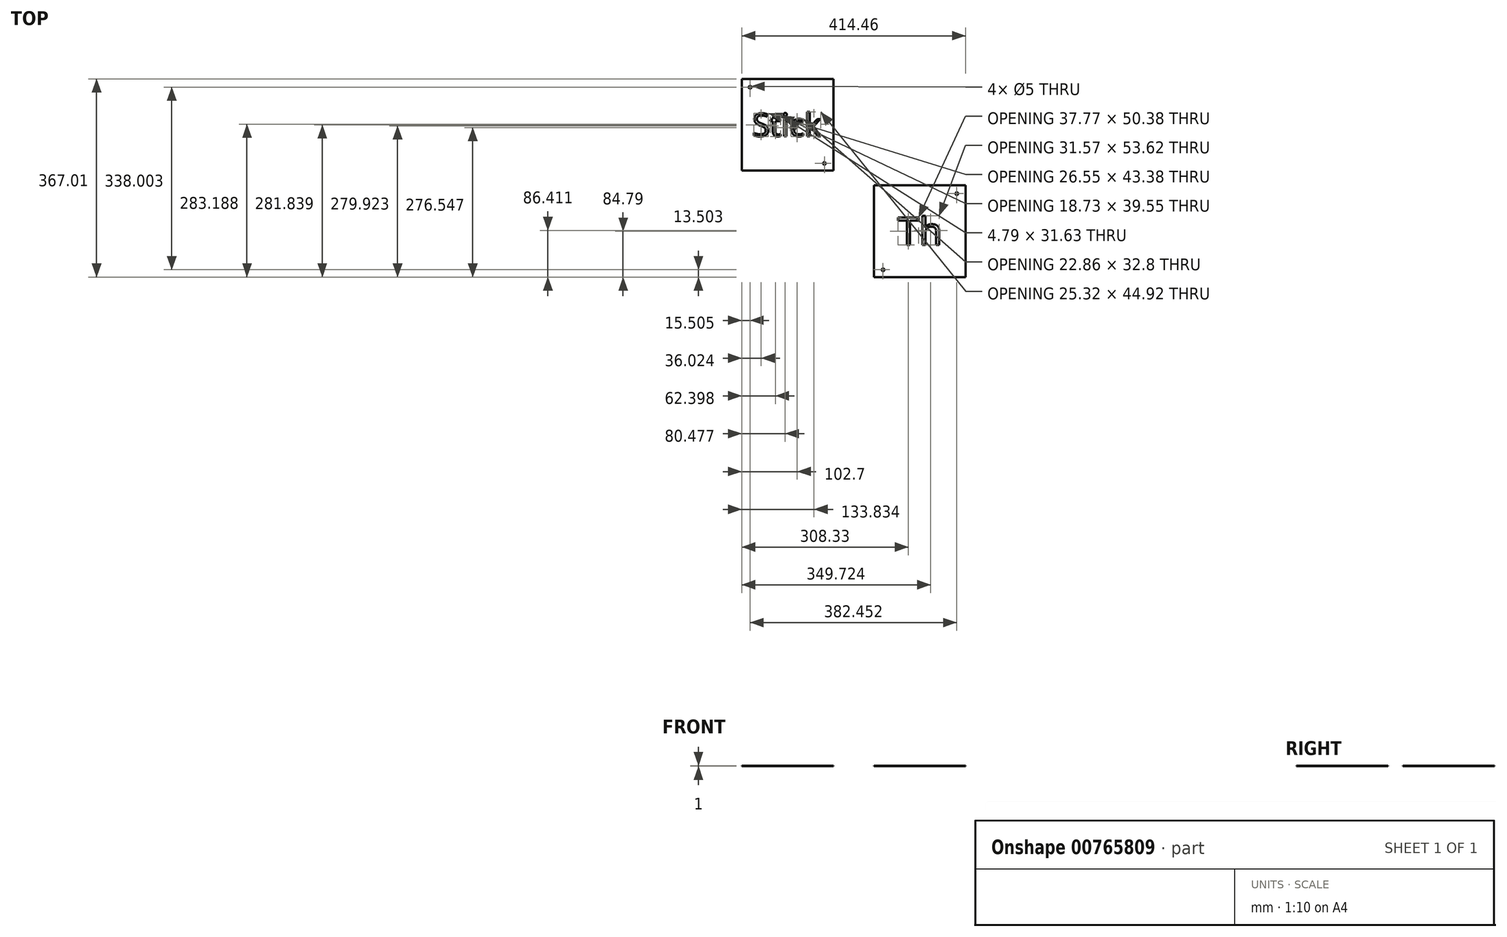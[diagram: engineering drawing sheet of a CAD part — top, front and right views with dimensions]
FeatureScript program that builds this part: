
annotation { "Feature Type Name" : "Feature", "Feature Type Description" : "" }
export const myFeature = defineFeature(function(context is Context, id is Id, definition is map)
    precondition{}
    {
        {
            var Q0;
            Q0=qCreatedBy(makeId("Top.planeOp"),FACE);
            var sketch = newSketch(context, id + "F0", { "sketchPlane" : qUnion([Q0])});
            skLineSegment(sketch, "E0.bottom", {"start": v(-144.03, 147.7) * mm, "end": v(25.97, 147.7) * mm});
            skLineSegment(sketch, "E0.top", {"start": v(-144.03, -22.3) * mm, "end": v(25.97, -22.3) * mm});
            skLineSegment(sketch, "E0.left", {"start": v(-144.03, 147.7) * mm, "end": v(-144.03, -22.3) * mm});
            skLineSegment(sketch, "E0.right", {"start": v(25.97, 147.7) * mm, "end": v(25.97, -22.3) * mm});
            skCircle(sketch, "E1", {"center": v(-128.53, 132.2) * mm, "radius": 2.5 * mm});
            skCircle(sketch, "E2", {"center": v(8.97, -8.8) * mm, "radius": 2.5 * mm});
            skText(sketch, "E3", { "text": "Stick", "fontName": "OpenSans-Regular.ttf"});
            const initialGuessF0  = {"E3": [-0.12434, 0.04142, 1, 0, 0.04256]};
            skSetInitialGuess(sketch, initialGuessF0);
            skSolve(sketch);
        }
        {
            var Q0;
            Q0=makeQuery(id+"F0.imprint","IMPRINT",FACE,{"disambiguationData":[TD([[makeQuery(id+"F0.imprint","IMPRINT",EDGE,{"derivedFrom":sQuery(id+"F0.wireOp",EDGE,"E0.bottom")}),-1.0]])]});
            extrude(context, id + "F1", {"entities" : qUnion([Q0]), "depth" : 1 * mm, "offsetDistance" : 25 * mm});
        }
        {
            var Q0;
            Q0=qCreatedBy(makeId("Top.planeOp"),FACE);
            var sketch = newSketch(context, id + "F2", { "sketchPlane" : qUnion([Q0])});
            skLineSegment(sketch, "E4.bottom", {"start": v(100.43, -49.3) * mm, "end": v(270.43, -49.3) * mm});
            skLineSegment(sketch, "E4.top", {"start": v(100.43, -219.3) * mm, "end": v(270.43, -219.3) * mm});
            skLineSegment(sketch, "E4.left", {"start": v(100.43, -49.3) * mm, "end": v(100.43, -219.3) * mm});
            skLineSegment(sketch, "E4.right", {"start": v(270.43, -49.3) * mm, "end": v(270.43, -219.3) * mm});
            skCircle(sketch, "E5", {"center": v(117.43, -205.8) * mm, "radius": 2.5 * mm});
            skCircle(sketch, "E6", {"center": v(253.93, -64.8) * mm, "radius": 2.5 * mm});
            skText(sketch, "E7", { "text": "Th", "fontName": "OpenSans-Regular.ttf"});
            const initialGuessF2  = {"E7": [0.1448, -0.15971, 1, 0, 0.05081]};
            skSetInitialGuess(sketch, initialGuessF2);
            skSolve(sketch);
        }
        {
            var Q0;
            Q0=makeQuery(id+"F2.imprint","IMPRINT",FACE,{"disambiguationData":[TD([[makeQuery(id+"F2.imprint","IMPRINT",EDGE,{"derivedFrom":sQuery(id+"F2.wireOp",EDGE,"E4.bottom")}),-1.0]])]});
            extrude(context, id + "F3", {"entities" : qUnion([Q0]), "depth" : 1 * mm, "offsetDistance" : 25 * mm});
        }
    });
